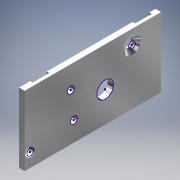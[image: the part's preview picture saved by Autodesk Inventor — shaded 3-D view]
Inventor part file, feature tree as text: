
AUTODESK INVENTOR PART (.ipt)
format: ipt  version: 2019 (Build 230136000, 136)  size: 144,896 bytes
history: native  units: mm
features: other x3, extrude x3, sketch x3, hole x2, fillet x1
ambient origin geometry x8: Origin, YZ Plane, XZ Plane, XY Plane, X Axis, Y Axis, Z Axis, Center Point
bodies: Body1 (feature_tree)
feature tree (12):
  other  "Bryła1"
  extrude  "Wyciągnięcie proste1"  Depth=25.0mm
  sketch  "Szkic2"
  hole  "Otwór1"  [1 undecoded]
  hole  "Otwór2"  [1 undecoded]
  extrude  "Wyciągnięcie proste2"  TaperAngle=0.0deg  [1 undecoded]
  sketch  "Szkic3"
  other  "Płaszczyzna konstrukcyjna1"
  other  "Płaszczyzna konstrukcyjna2"
  extrude  "Wyciągnięcie proste3"  Depth=10.0mm TaperAngle=0.0deg
  fillet  "Zaokrąglenie1"  Radius=1.0mm
  sketch  "Szkic1"
note: 3 required parameter values undecoded (feature->parameter linkage not recoverable at this tier; creation-order binding heuristic only, values carry confidence <= 0.55)
